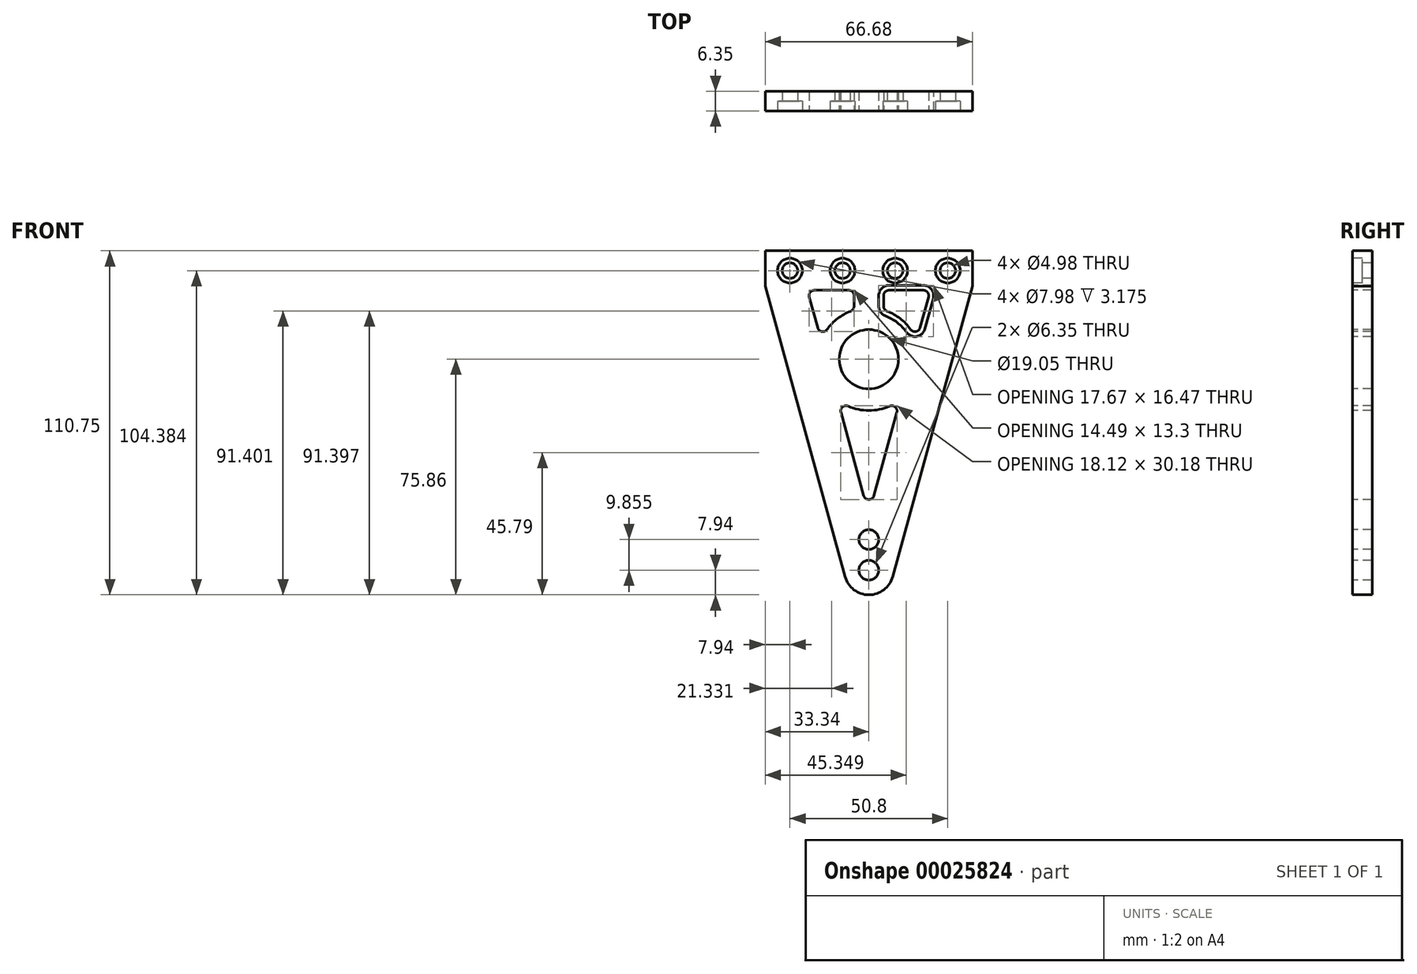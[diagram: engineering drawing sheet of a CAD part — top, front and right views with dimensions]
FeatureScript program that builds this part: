
annotation { "Feature Type Name" : "Feature", "Feature Type Description" : "" }
export const myFeature = defineFeature(function(context is Context, id is Id, definition is map)
    precondition{}
    {
        {
            var Q0;
            Q0=qCreatedBy(makeId("Front.planeOp"),FACE);
            var sketch = newSketch(context, id + "F0", { "sketchPlane" : qUnion([Q0])});
            skCircle(sketch, "E0", {"center": v(0, 0) * mm, "radius": 11.11 * mm});
            skLineSegment(sketch, "E1", {"start": v(0, 54.86) * mm, "end": v(0, 0) * mm, "construction": true});
            skLineSegment(sketch, "E2", {"start": v(0, 0) * mm, "end": v(80.81, 0) * mm, "construction": true});
            skLineSegment(sketch, "E3.bottom", {"start": v(-31.75, 33.3) * mm, "end": v(31.75, 33.3) * mm});
            skLineSegment(sketch, "E3.left", {"start": v(-31.75, 33.3) * mm, "end": v(-31.75, 23.77) * mm});
            skLineSegment(sketch, "E3.right", {"start": v(31.75, 33.3) * mm, "end": v(31.75, 23.77) * mm});
            skLineSegment(sketch, "E4", {"start": v(-31.75, 23.77) * mm, "end": v(-6.12, -69.6) * mm});
            skLineSegment(sketch, "E5", {"start": v(6.12, -69.6) * mm, "end": v(31.75, 23.77) * mm});
            skArc(sketch, "E6", {"start": v(-6.12, -69.6) * mm, "mid": v(0, -74.27) * mm, "end": v(6.12, -69.6) * mm});
            skSolve(sketch);
        }
        {
            var Q0;
            Q0=makeQuery(id+"F0.imprint","IMPRINT",FACE,{"disambiguationData":[TD([[makeQuery(id+"F0.imprint","IMPRINT",EDGE,{"derivedFrom":sQuery(id+"F0.wireOp",EDGE,"E0")}),-1.0]])]});
            extrude(context, id + "F1", {"entities" : qUnion([Q0]), "depth" : 6.35 * mm});
        }
        {
            var Q0;
            Q0=makeQuery(id+"F1.opExtrude","CAP_FACE",FACE,{"disambiguationData":[OSD([sQuery(id+"F0.wireOp",EDGE,"E0"),sQuery(id+"F0.wireOp",EDGE,"E3.bottom"),sQuery(id+"F0.wireOp",EDGE,"E3.left"),sQuery(id+"F0.wireOp",EDGE,"E3.right"),sQuery(id+"F0.wireOp",EDGE,"E4"),sQuery(id+"F0.wireOp",EDGE,"E5"),sQuery(id+"F0.wireOp",EDGE,"E6")])],"isStart":false});
            var sketch = newSketch(context, id + "F2", { "sketchPlane" : qUnion([Q0])});
            skLineSegment(sketch, "E7.0", {"start": v(21.87, 23.77) * mm, "end": v(3.17, 23.77) * mm});
            skLineSegment(sketch, "E7.1", {"start": v(0, -55.92) * mm, "end": v(13.77, -5.75) * mm});
            skLineSegment(sketch, "E7.2", {"start": v(-21.87, 23.77) * mm, "end": v(-14.78, -2.08) * mm});
            skArc(sketch, "E8", {"start": v(-13.77, -5.75) * mm, "mid": v(0, -14.92) * mm, "end": v(13.77, -5.75) * mm});
            skLineSegment(sketch, "E9.trimOffspring", {"start": v(-13.77, -5.75) * mm, "end": v(0, -55.92) * mm});
            skArc(sketch, "E10.trimOffspring", {"start": v(14.78, -2.08) * mm, "mid": v(12.25, 8.53) * mm, "end": v(3.18, 14.58) * mm});
            skLineSegment(sketch, "E11.trimOffspring", {"start": v(14.78, -2.08) * mm, "end": v(21.87, 23.77) * mm});
            skLineSegment(sketch, "E12", {"start": v(0, 0) * mm, "end": v(0, 52.94) * mm, "construction": true});
            skLineSegment(sketch, "E13", {"start": v(-3.17, 23.77) * mm, "end": v(-3.18, 14.58) * mm});
            skLineSegment(sketch, "E14", {"start": v(3.17, 23.77) * mm, "end": v(3.18, 14.58) * mm});
            skArc(sketch, "E15.trimOffspring", {"start": v(-3.18, 14.58) * mm, "mid": v(-12.25, 8.53) * mm, "end": v(-14.78, -2.08) * mm});
            skLineSegment(sketch, "E16.trimOffspring", {"start": v(-3.17, 23.77) * mm, "end": v(-21.87, 23.77) * mm});
            skSolve(sketch);
        }
        {
            var Q0;
            Q0=makeQuery(id+"F2.imprint","IMPRINT",FACE,{"disambiguationData":[TD([[makeQuery(id+"F2.imprint","IMPRINT",EDGE,{"derivedFrom":sQuery(id+"F2.wireOp",EDGE,"E7.2")}),1.0]])]});
            var Q1;
            Q1=makeQuery(id+"F2.imprint","IMPRINT",FACE,{"disambiguationData":[TD([[makeQuery(id+"F2.imprint","IMPRINT",EDGE,{"derivedFrom":sQuery(id+"F2.wireOp",EDGE,"E7.0")}),1.0]])]});
            var Q2;
            Q2=makeQuery(id+"F2.imprint","IMPRINT",FACE,{"disambiguationData":[TD([[makeQuery(id+"F2.imprint","IMPRINT",EDGE,{"derivedFrom":sQuery(id+"F2.wireOp",EDGE,"E7.1")}),1.0]])]});
            extrude(context, id + "F3", {"entities" : qUnion([Q0, Q1, Q2]), "operationType" : NewBodyOperationType.REMOVE, "endBound" : BoundingType.THROUGH_ALL, "oppositeDirection" : true, "depth" : 25.4 * mm});
        }
        {
            var Q0;
            Q0=makeQuery(id+"F3.boolean.opBoolean","COPY",EDGE,{"derivedFrom":makeQuery(id+"F3.opExtrude","SWEPT_EDGE",EDGE,{"disambiguationData":[OSD([sQuery(id+"F2.wireOp",EDGE,"E7.2"),sQuery(id+"F2.wireOp",EDGE,"E15.trimOffspring")])]})});
            var Q1;
            Q1=makeQuery(id+"F3.boolean.opBoolean","COPY",EDGE,{"derivedFrom":makeQuery(id+"F3.opExtrude","SWEPT_EDGE",EDGE,{"disambiguationData":[OSD([sQuery(id+"F2.wireOp",EDGE,"E7.1"),sQuery(id+"F2.wireOp",EDGE,"E9.trimOffspring")])]})});
            var Q2;
            Q2=makeQuery(id+"F3.boolean.opBoolean","COPY",EDGE,{"derivedFrom":makeQuery(id+"F3.opExtrude","SWEPT_EDGE",EDGE,{"disambiguationData":[OSD([sQuery(id+"F2.wireOp",EDGE,"E7.1"),sQuery(id+"F2.wireOp",EDGE,"E8")])]})});
            var Q3;
            Q3=makeQuery(id+"F3.boolean.opBoolean","COPY",EDGE,{"derivedFrom":makeQuery(id+"F3.opExtrude","SWEPT_EDGE",EDGE,{"disambiguationData":[OSD([sQuery(id+"F2.wireOp",EDGE,"E8"),sQuery(id+"F2.wireOp",EDGE,"E9.trimOffspring")])]})});
            var Q4;
            Q4=makeQuery(id+"F3.boolean.opBoolean","COPY",EDGE,{"derivedFrom":makeQuery(id+"F3.opExtrude","SWEPT_EDGE",EDGE,{"disambiguationData":[OSD([sQuery(id+"F2.wireOp",EDGE,"E7.0"),sQuery(id+"F2.wireOp",EDGE,"E14")])]})});
            var Q5;
            Q5=makeQuery(id+"F3.boolean.opBoolean","COPY",EDGE,{"derivedFrom":makeQuery(id+"F3.opExtrude","SWEPT_EDGE",EDGE,{"disambiguationData":[OSD([sQuery(id+"F2.wireOp",EDGE,"E13"),sQuery(id+"F2.wireOp",EDGE,"E16.trimOffspring")])]})});
            var Q6;
            Q6=makeQuery(id+"F3.boolean.opBoolean","COPY",EDGE,{"derivedFrom":makeQuery(id+"F3.opExtrude","SWEPT_EDGE",EDGE,{"disambiguationData":[OSD([sQuery(id+"F2.wireOp",EDGE,"E7.0"),sQuery(id+"F2.wireOp",EDGE,"E11.trimOffspring")])]})});
            var Q7;
            Q7=makeQuery(id+"F3.boolean.opBoolean","COPY",EDGE,{"derivedFrom":makeQuery(id+"F3.opExtrude","SWEPT_EDGE",EDGE,{"disambiguationData":[OSD([sQuery(id+"F2.wireOp",EDGE,"E7.2"),sQuery(id+"F2.wireOp",EDGE,"E16.trimOffspring")])]})});
            var Q8;
            Q8=makeQuery(id+"F3.boolean.opBoolean","COPY",EDGE,{"derivedFrom":makeQuery(id+"F3.opExtrude","SWEPT_EDGE",EDGE,{"disambiguationData":[OSD([sQuery(id+"F2.wireOp",EDGE,"E10.trimOffspring"),sQuery(id+"F2.wireOp",EDGE,"E11.trimOffspring")])]})});
            var Q9;
            Q9=makeQuery(id+"F3.boolean.opBoolean","COPY",EDGE,{"derivedFrom":makeQuery(id+"F3.opExtrude","SWEPT_EDGE",EDGE,{"disambiguationData":[OSD([sQuery(id+"F2.wireOp",EDGE,"E10.trimOffspring"),sQuery(id+"F2.wireOp",EDGE,"E14")])]})});
            var Q10;
            Q10=makeQuery(id+"F3.boolean.opBoolean","COPY",EDGE,{"derivedFrom":makeQuery(id+"F3.opExtrude","SWEPT_EDGE",EDGE,{"disambiguationData":[OSD([sQuery(id+"F2.wireOp",EDGE,"E13"),sQuery(id+"F2.wireOp",EDGE,"E15.trimOffspring")])]})});
            fillet(context, id + "F4", {"entities" : qUnion([Q0, Q1, Q2, Q3, Q4, Q5, Q6, Q7, Q8, Q9, Q10]), "radius" : 3.3 * mm, "tangentPropagation" : true, "allowEdgeOverflow" : false});
        }
        {
            var Q0;
            Q0=makeQuery(id+"F1.opExtrude","CAP_FACE",FACE,{"disambiguationData":[OSD([sQuery(id+"F0.wireOp",EDGE,"E0"),sQuery(id+"F0.wireOp",EDGE,"E3.bottom"),sQuery(id+"F0.wireOp",EDGE,"E3.left"),sQuery(id+"F0.wireOp",EDGE,"E3.right"),sQuery(id+"F0.wireOp",EDGE,"E4"),sQuery(id+"F0.wireOp",EDGE,"E5"),sQuery(id+"F0.wireOp",EDGE,"E6")])],"isStart":false});
            var sketch = newSketch(context, id + "F5", { "sketchPlane" : qUnion([Q0])});
            skLineSegment(sketch, "E17", {"start": v(-25.4, 28.52) * mm, "end": v(25.4, 28.52) * mm});
            skLineSegment(sketch, "E18", {"start": v(0, -67.92) * mm, "end": v(0, 28.52) * mm});
            skPoint(sketch, "E19", {"position": v(-8.47, 28.52) * mm});
            skPoint(sketch, "E20", {"position": v(8.47, 28.52) * mm});
            skPoint(sketch, "E21", {"position": v(0, -58.06) * mm});
            skSolve(sketch);
        }
        {
            var Q0;
            Q0=sQuery(id+"F5.wireOp",VERTEX,"E17.end");
            var Q1;
            Q1=sQuery(id+"F5.wireOp",VERTEX,"E20");
            var Q2;
            Q2=sQuery(id+"F5.wireOp",VERTEX,"E19");
            var Q3;
            Q3=sQuery(id+"F5.wireOp",VERTEX,"E17.start");
            var Q4;
            Q4=makeQuery(id+"F1.opExtrude","SWEPT_BODY",BODY,{"disambiguationData":[OSD([sQuery(id+"F0.wireOp",EDGE,"E0"),sQuery(id+"F0.wireOp",EDGE,"E3.bottom"),sQuery(id+"F0.wireOp",EDGE,"E3.left"),sQuery(id+"F0.wireOp",EDGE,"E3.right"),sQuery(id+"F0.wireOp",EDGE,"E4"),sQuery(id+"F0.wireOp",EDGE,"E5"),sQuery(id+"F0.wireOp",EDGE,"E6")])]});
            hole(context, id + "F6", {"style" : HoleStyle.C_BORE, "holeDiameter" : 4.98 * mm, "cBoreDiameter" : 7.98 * mm, "cBoreDepth" : 3.17 * mm, "endStyle" : HoleEndStyle.THROUGH, "locations" : qUnion([Q0, Q1, Q2, Q3]), "scope" : qUnion([Q4])});
        }
        {
            var Q0;
            Q0=sQuery(id+"F5.wireOp",VERTEX,"E21");
            var Q1;
            Q1=sQuery(id+"F5.wireOp",VERTEX,"E18.start");
            var Q2;
            Q2=makeQuery(id+"F1.opExtrude","SWEPT_BODY",BODY,{"disambiguationData":[OSD([sQuery(id+"F0.wireOp",EDGE,"E0"),sQuery(id+"F0.wireOp",EDGE,"E3.bottom"),sQuery(id+"F0.wireOp",EDGE,"E3.left"),sQuery(id+"F0.wireOp",EDGE,"E3.right"),sQuery(id+"F0.wireOp",EDGE,"E4"),sQuery(id+"F0.wireOp",EDGE,"E5"),sQuery(id+"F0.wireOp",EDGE,"E6")])]});
            hole(context, id + "F7", {"style" : HoleStyle.SIMPLE, "holeDiameter" : 6.35 * mm, "endStyle" : HoleEndStyle.THROUGH, "locations" : qUnion([Q0, Q1]), "scope" : qUnion([Q2])});
        }
        {
            var Q0;
            Q0=makeQuery(id+"F1.opExtrude","CAP_FACE",FACE,{"disambiguationData":[OSD([sQuery(id+"F0.wireOp",EDGE,"E0"),sQuery(id+"F0.wireOp",EDGE,"E3.bottom"),sQuery(id+"F0.wireOp",EDGE,"E3.left"),sQuery(id+"F0.wireOp",EDGE,"E3.right"),sQuery(id+"F0.wireOp",EDGE,"E4"),sQuery(id+"F0.wireOp",EDGE,"E5"),sQuery(id+"F0.wireOp",EDGE,"E6")])],"isStart":false});
            var sketch = newSketch(context, id + "F8", { "sketchPlane" : qUnion([Q0])});
            skLineSegment(sketch, "E22.0", {"start": v(33.34, 34.89) * mm, "end": v(-33.34, 34.89) * mm});
            skLineSegment(sketch, "E22.1", {"start": v(33.34, 23.56) * mm, "end": v(33.34, 34.89) * mm});
            skLineSegment(sketch, "E22.2", {"start": v(7.65, -70.02) * mm, "end": v(33.34, 23.56) * mm});
            skArc(sketch, "E22.3", {"start": v(-7.65, -70.02) * mm, "mid": v(0, -75.86) * mm, "end": v(7.65, -70.02) * mm});
            skLineSegment(sketch, "E22.4", {"start": v(-33.34, 23.56) * mm, "end": v(-7.65, -70.02) * mm});
            skLineSegment(sketch, "E22.5", {"start": v(-33.34, 34.89) * mm, "end": v(-33.34, 23.56) * mm});
            skLineSegment(sketch, "E23.0.0", {"start": v(31.75, 33.3) * mm, "end": v(-31.75, 33.3) * mm});
            skLineSegment(sketch, "E23.0.1", {"start": v(-31.75, 33.3) * mm, "end": v(-31.75, 23.77) * mm});
            skLineSegment(sketch, "E23.0.2", {"start": v(-31.75, 23.77) * mm, "end": v(-6.12, -69.6) * mm});
            skArc(sketch, "E23.0.3", {"start": v(-6.12, -69.6) * mm, "mid": v(0, -74.27) * mm, "end": v(6.12, -69.6) * mm});
            skLineSegment(sketch, "E23.0.4", {"start": v(6.12, -69.6) * mm, "end": v(31.75, 23.77) * mm});
            skLineSegment(sketch, "E23.0.5", {"start": v(31.75, 23.77) * mm, "end": v(31.75, 33.3) * mm});
            skLineSegment(sketch, "E24.0", {"start": v(-6.48, 23.77) * mm, "end": v(-17.54, 23.77) * mm});
            skArc(sketch, "E24.1", {"start": v(-6.48, 23.77) * mm, "mid": v(-4.14, 22.8) * mm, "end": v(-3.17, 20.47) * mm});
            skLineSegment(sketch, "E24.2", {"start": v(-3.17, 20.47) * mm, "end": v(-3.18, 17.03) * mm});
            skArc(sketch, "E24.3", {"start": v(-3.18, 17.03) * mm, "mid": v(-3.76, 15.16) * mm, "end": v(-5.3, 13.95) * mm});
            skArc(sketch, "E24.4", {"start": v(-5.3, 13.95) * mm, "mid": v(-9.11, 11.82) * mm, "end": v(-12.14, 8.67) * mm});
            skArc(sketch, "E24.5", {"start": v(-12.14, 8.67) * mm, "mid": v(-15.4, 7.34) * mm, "end": v(-18.01, 9.72) * mm});
            skLineSegment(sketch, "E24.6", {"start": v(-20.73, 19.6) * mm, "end": v(-18.01, 9.72) * mm});
            skArc(sketch, "E24.7", {"start": v(-20.73, 19.6) * mm, "mid": v(-20.17, 22.47) * mm, "end": v(-17.54, 23.77) * mm});
            skArc(sketch, "E25.0", {"start": v(17.54, 22.19) * mm, "mid": v(18.9, 21.51) * mm, "end": v(19.2, 20.02) * mm});
            skLineSegment(sketch, "E25.1", {"start": v(16.48, 10.14) * mm, "end": v(19.2, 20.02) * mm});
            skArc(sketch, "E25.2", {"start": v(16.48, 10.14) * mm, "mid": v(15.13, 8.9) * mm, "end": v(13.44, 9.6) * mm});
            skArc(sketch, "E25.3", {"start": v(13.44, 9.6) * mm, "mid": v(10.08, 13.07) * mm, "end": v(5.87, 15.43) * mm});
            skArc(sketch, "E25.4", {"start": v(5.87, 15.43) * mm, "mid": v(5.07, 16.06) * mm, "end": v(4.76, 17.03) * mm});
            skLineSegment(sketch, "E25.5", {"start": v(17.54, 22.19) * mm, "end": v(6.48, 22.19) * mm});
            skLineSegment(sketch, "E25.6", {"start": v(4.76, 20.47) * mm, "end": v(4.76, 17.03) * mm});
            skArc(sketch, "E25.7", {"start": v(4.76, 20.47) * mm, "mid": v(5.26, 21.68) * mm, "end": v(6.48, 22.19) * mm});
            skLineSegment(sketch, "E26.0", {"start": v(-6.48, 22.19) * mm, "end": v(-17.54, 22.19) * mm});
            skArc(sketch, "E26.1", {"start": v(-19.2, 20.02) * mm, "mid": v(-18.9, 21.51) * mm, "end": v(-17.54, 22.19) * mm});
            skLineSegment(sketch, "E26.2", {"start": v(-19.2, 20.02) * mm, "end": v(-16.48, 10.14) * mm});
            skArc(sketch, "E26.3", {"start": v(-13.44, 9.6) * mm, "mid": v(-15.13, 8.9) * mm, "end": v(-16.48, 10.14) * mm});
            skArc(sketch, "E26.4", {"start": v(-5.87, 15.43) * mm, "mid": v(-10.08, 13.07) * mm, "end": v(-13.44, 9.6) * mm});
            skArc(sketch, "E26.5", {"start": v(-6.48, 22.19) * mm, "mid": v(-5.26, 21.68) * mm, "end": v(-4.76, 20.47) * mm});
            skArc(sketch, "E26.6", {"start": v(-4.76, 17.03) * mm, "mid": v(-5.07, 16.06) * mm, "end": v(-5.87, 15.43) * mm});
            skLineSegment(sketch, "E26.7", {"start": v(-4.76, 20.47) * mm, "end": v(-4.76, 17.03) * mm});
            skCircle(sketch, "E27.0", {"center": v(0, 0) * mm, "radius": 11.11 * mm});
            skCircle(sketch, "E28.0", {"center": v(0, 0) * mm, "radius": 9.53 * mm});
            skArc(sketch, "E29.0", {"start": v(-6.66, -15.1) * mm, "mid": v(0, -16.51) * mm, "end": v(6.66, -15.1) * mm});
            skArc(sketch, "E29.1", {"start": v(-9, -17.13) * mm, "mid": v(-8.47, -15.38) * mm, "end": v(-6.66, -15.1) * mm});
            skLineSegment(sketch, "E29.2", {"start": v(-9, -17.13) * mm, "end": v(-1.65, -43.9) * mm});
            skArc(sketch, "E29.3", {"start": v(1.65, -43.9) * mm, "mid": v(0, -45.16) * mm, "end": v(-1.65, -43.9) * mm});
            skLineSegment(sketch, "E29.4", {"start": v(1.65, -43.9) * mm, "end": v(9, -17.13) * mm});
            skArc(sketch, "E29.5", {"start": v(6.66, -15.1) * mm, "mid": v(8.47, -15.38) * mm, "end": v(9, -17.13) * mm});
            skArc(sketch, "E30.0", {"start": v(-6.02, -13.66) * mm, "mid": v(0, -14.92) * mm, "end": v(6.02, -13.66) * mm});
            skArc(sketch, "E31.0", {"start": v(6.02, -13.66) * mm, "mid": v(9.5, -14.18) * mm, "end": v(10.53, -17.55) * mm});
            skLineSegment(sketch, "E32.0", {"start": v(3.18, -44.32) * mm, "end": v(10.53, -17.55) * mm});
            skArc(sketch, "E33.0", {"start": v(3.18, -44.32) * mm, "mid": v(0, -46.75) * mm, "end": v(-3.18, -44.32) * mm});
            skLineSegment(sketch, "E34.0", {"start": v(-10.53, -17.55) * mm, "end": v(-3.18, -44.32) * mm});
            skArc(sketch, "E35.0", {"start": v(-10.53, -17.55) * mm, "mid": v(-9.5, -14.18) * mm, "end": v(-6.02, -13.66) * mm});
            skLineSegment(sketch, "E36.0", {"start": v(18.01, 9.72) * mm, "end": v(20.73, 19.6) * mm});
            skArc(sketch, "E37.0", {"start": v(18.01, 9.72) * mm, "mid": v(15.4, 7.34) * mm, "end": v(12.14, 8.67) * mm});
            skArc(sketch, "E38.0", {"start": v(12.14, 8.67) * mm, "mid": v(9.11, 11.82) * mm, "end": v(5.3, 13.95) * mm});
            skArc(sketch, "E39.0", {"start": v(5.3, 13.95) * mm, "mid": v(3.76, 15.16) * mm, "end": v(3.18, 17.03) * mm});
            skArc(sketch, "E40.0", {"start": v(17.54, 23.77) * mm, "mid": v(20.17, 22.47) * mm, "end": v(20.73, 19.6) * mm});
            skLineSegment(sketch, "E41.0", {"start": v(17.54, 23.77) * mm, "end": v(6.48, 23.77) * mm});
            skArc(sketch, "E42.0", {"start": v(3.17, 20.47) * mm, "mid": v(4.14, 22.8) * mm, "end": v(6.48, 23.77) * mm});
            skLineSegment(sketch, "E43.0", {"start": v(3.18, 20.47) * mm, "end": v(3.18, 17.03) * mm});
            skSolve(sketch);
        }
        {
            var Q0;
            Q0=makeQuery(id+"F8.imprint","IMPRINT",FACE,{"disambiguationData":[TD([[makeQuery(id+"F8.imprint","IMPRINT",EDGE,{"derivedFrom":sQuery(id+"F8.wireOp",EDGE,"E22.0")}),1.0]])]});
            var Q1;
            Q1=makeQuery(id+"F8.imprint","IMPRINT",FACE,{"disambiguationData":[TD([[makeQuery(id+"F8.imprint","IMPRINT",EDGE,{"derivedFrom":sQuery(id+"F8.wireOp",EDGE,"E24.0")}),1.0]])]});
            var Q2;
            Q2=makeQuery(id+"F8.imprint","IMPRINT",FACE,{"disambiguationData":[TD([[makeQuery(id+"F8.imprint","IMPRINT",EDGE,{"derivedFrom":sQuery(id+"F8.wireOp",EDGE,"E25.0")}),1.0]])]});
            var Q3;
            Q3=makeQuery(id+"F8.imprint","IMPRINT",FACE,{"disambiguationData":[TD([[makeQuery(id+"F8.imprint","IMPRINT",EDGE,{"derivedFrom":sQuery(id+"F8.wireOp",EDGE,"E27.0")}),1.0]])]});
            var Q4;
            Q4=makeQuery(id+"F8.imprint","IMPRINT",FACE,{"disambiguationData":[TD([[makeQuery(id+"F8.imprint","IMPRINT",EDGE,{"derivedFrom":sQuery(id+"F8.wireOp",EDGE,"E29.0")}),1.0]])]});
            var Q5;
            Q5=makeQuery(id+"F1.opExtrude","CAP_FACE",FACE,{"disambiguationData":[OSD([sQuery(id+"F0.wireOp",EDGE,"E0"),sQuery(id+"F0.wireOp",EDGE,"E3.bottom"),sQuery(id+"F0.wireOp",EDGE,"E3.left"),sQuery(id+"F0.wireOp",EDGE,"E3.right"),sQuery(id+"F0.wireOp",EDGE,"E4"),sQuery(id+"F0.wireOp",EDGE,"E5"),sQuery(id+"F0.wireOp",EDGE,"E6")])],"isStart":true});
            extrude(context, id + "F9", {"entities" : qUnion([Q0, Q1, Q2, Q3, Q4]), "operationType" : NewBodyOperationType.ADD, "endBound" : BoundingType.UP_TO_SURFACE, "oppositeDirection" : true, "endBoundEntityFace" : qUnion([Q5]), "depth" : 25.4 * mm});
        }
    });
